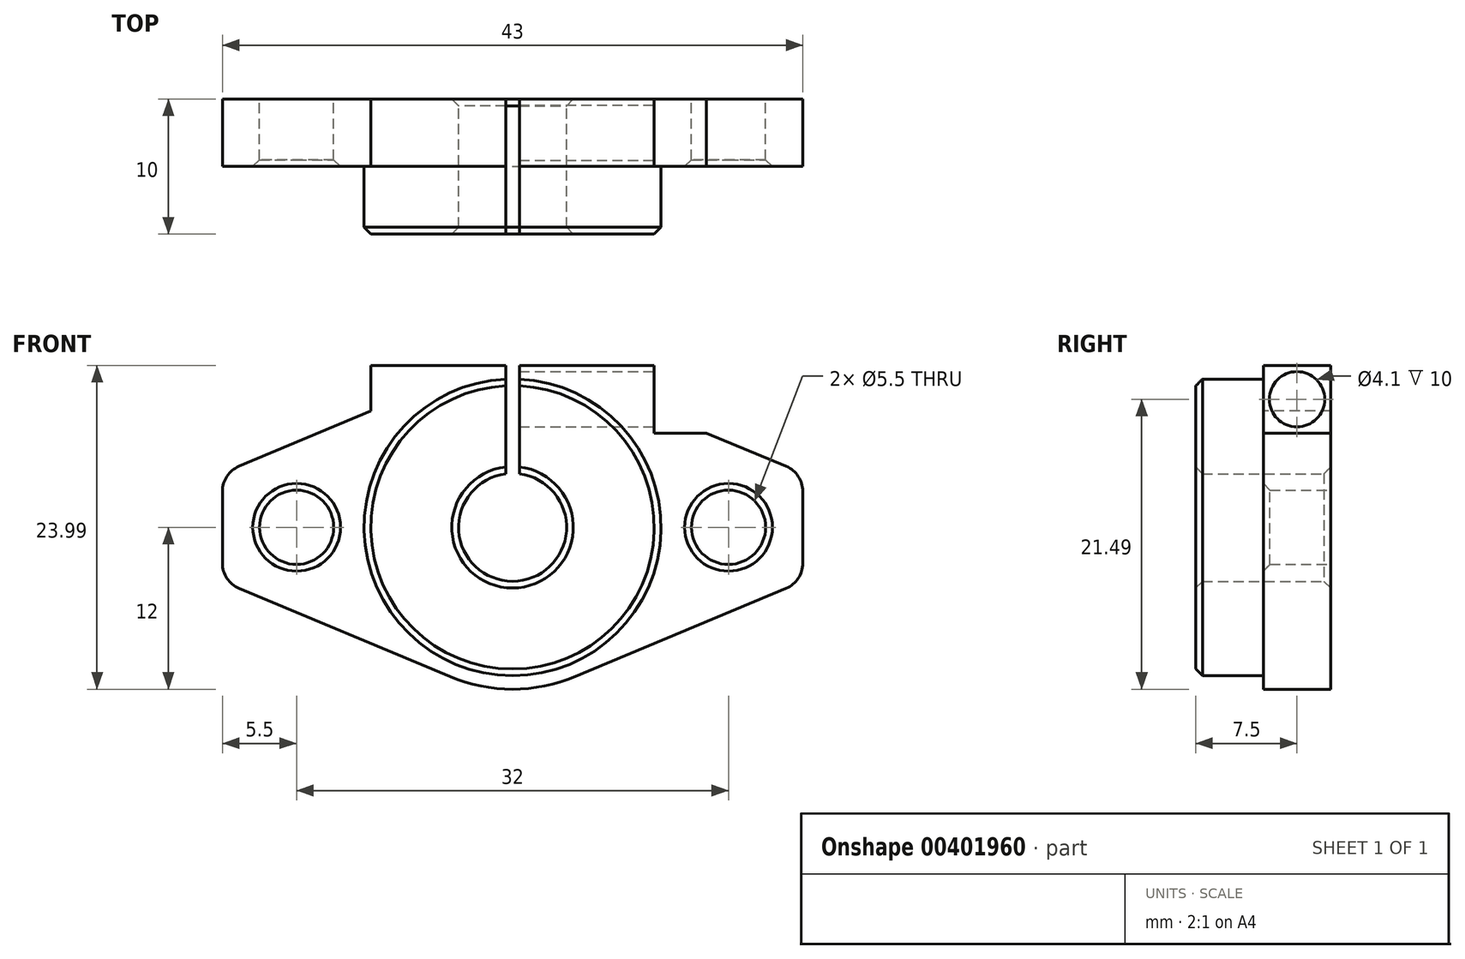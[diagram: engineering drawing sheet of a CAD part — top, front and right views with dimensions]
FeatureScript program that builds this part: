
annotation { "Feature Type Name" : "Feature", "Feature Type Description" : "" }
export const myFeature = defineFeature(function(context is Context, id is Id, definition is map)
    precondition{}
    {
        {
            var Q0;
            Q0=qCreatedBy(makeId("Front.planeOp"),FACE);
            var sketch = newSketch(context, id + "F0", { "sketchPlane" : qUnion([Q0])});
            skLineSegment(sketch, "E0.bottom", {"start": v(-21.5, 12) * mm, "end": v(21.5, 12) * mm, "construction": true});
            skLineSegment(sketch, "E0.top", {"start": v(-21.5, -12) * mm, "end": v(21.5, -12) * mm, "construction": true});
            skLineSegment(sketch, "E0.left", {"start": v(-21.5, 12) * mm, "end": v(-21.5, -12) * mm, "construction": true});
            skLineSegment(sketch, "E0.right", {"start": v(21.5, 12) * mm, "end": v(21.5, -12) * mm, "construction": true});
            skLineSegment(sketch, "E1", {"start": v(0, 0) * mm, "end": v(0, 12) * mm, "construction": true});
            skLineSegment(sketch, "E2", {"start": v(0, 0) * mm, "end": v(-21.5, 0) * mm, "construction": true});
            skCircle(sketch, "E3", {"center": v(-16, 0) * mm, "radius": 2.75 * mm});
            skCircle(sketch, "E4.MirrorC", {"center": v(16, 0) * mm, "radius": 2.75 * mm});
            skLineSegment(sketch, "E5", {"start": v(-21.5, -4) * mm, "end": v(-21.5, 4) * mm});
            skCircle(sketch, "E6", {"center": v(0, 0) * mm, "radius": 4 * mm});
            skArc(sketch, "E7", {"start": v(-4.64, -11.07) * mm, "mid": v(0, -12) * mm, "end": v(4.64, -11.07) * mm});
            skLineSegment(sketch, "E8", {"start": v(-21.5, 4) * mm, "end": v(-4.64, 11.07) * mm});
            skLineSegment(sketch, "E9", {"start": v(-21.5, -4) * mm, "end": v(-4.64, -11.07) * mm});
            skLineSegment(sketch, "E10.MirrorCS", {"start": v(21.5, 4) * mm, "end": v(4.64, 11.07) * mm});
            skLineSegment(sketch, "E11.MirrorCS", {"start": v(21.5, -4) * mm, "end": v(21.5, 4) * mm});
            skLineSegment(sketch, "E12.MirrorCS", {"start": v(21.5, -4) * mm, "end": v(4.64, -11.07) * mm});
            skArc(sketch, "E13.trimOffspring", {"start": v(4.64, 11.07) * mm, "mid": v(0, 12) * mm, "end": v(-4.64, 11.07) * mm});
            skSolve(sketch);
        }
        {
            var Q0;
            Q0=makeQuery(id+"F0.imprint","IMPRINT",FACE,{"disambiguationData":[TD([[makeQuery(id+"F0.imprint","IMPRINT",EDGE,{"derivedFrom":sQuery(id+"F0.wireOp",EDGE,"E3")}),-1.0]])]});
            extrude(context, id + "F1", {"entities" : qUnion([Q0]), "depth" : 5 * mm});
        }
        {
            var Q0;
            Q0=makeQuery(id+"F1.opExtrude","CAP_FACE",FACE,{"disambiguationData":[OSD([sQuery(id+"F0.wireOp",EDGE,"E3"),sQuery(id+"F0.wireOp",EDGE,"E4.MirrorC"),sQuery(id+"F0.wireOp",EDGE,"E5"),sQuery(id+"F0.wireOp",EDGE,"E6"),sQuery(id+"F0.wireOp",EDGE,"E7"),sQuery(id+"F0.wireOp",EDGE,"E8"),sQuery(id+"F0.wireOp",EDGE,"E9"),sQuery(id+"F0.wireOp",EDGE,"E10.MirrorCS"),sQuery(id+"F0.wireOp",EDGE,"E11.MirrorCS"),sQuery(id+"F0.wireOp",EDGE,"E12.MirrorCS"),sQuery(id+"F0.wireOp",EDGE,"E13.trimOffspring")])],"isStart":false});
            var sketch = newSketch(context, id + "F2", { "sketchPlane" : qUnion([Q0])});
            skCircle(sketch, "E14", {"center": v(0, 0) * mm, "radius": 11 * mm});
            skCircle(sketch, "E15.0", {"center": v(0, 0) * mm, "radius": 4 * mm});
            skSolve(sketch);
        }
        {
            var Q0;
            Q0 = qSketchRegion(id + "F2", true);
            extrude(context, id + "F3", {"entities" : qUnion([Q0]), "operationType" : NewBodyOperationType.ADD, "depth" : 5 * mm});
        }
        {
            var Q0;
            Q0=makeQuery(id+"F3.opExtrude","CAP_FACE",FACE,{"disambiguationData":[OSD([sQuery(id+"F2.wireOp",EDGE,"E14"),sQuery(id+"F2.wireOp",EDGE,"E15.0")])],"isStart":false});
            var sketch = newSketch(context, id + "F4", { "sketchPlane" : qUnion([Q0])});
            skLineSegment(sketch, "E16.bottom", {"start": v(-0.5, 18) * mm, "end": v(0.5, 18) * mm});
            skLineSegment(sketch, "E16.top", {"start": v(-0.5, 0) * mm, "end": v(0.5, 0) * mm});
            skLineSegment(sketch, "E16.left", {"start": v(-0.5, 18) * mm, "end": v(-0.5, 0) * mm});
            skLineSegment(sketch, "E16.right", {"start": v(0.5, 18) * mm, "end": v(0.5, 0) * mm});
            skSolve(sketch);
        }
        {
            var Q0;
            Q0 = qSketchRegion(id + "F4", true);
            extrude(context, id + "F5", {"entities" : qUnion([Q0]), "operationType" : NewBodyOperationType.REMOVE, "endBound" : BoundingType.THROUGH_ALL, "oppositeDirection" : true, "depth" : 25 * mm});
        }
        {
            var Q0;
            {var subQ0=sQuery(id+"F0.wireOp",EDGE,"E8");var subQ1=sQuery(id+"F0.wireOp",EDGE,"E7");var subQ2=sQuery(id+"F0.wireOp",EDGE,"E5");var subQ3=sQuery(id+"F0.wireOp",EDGE,"E3");var subQ4=sQuery(id+"F0.wireOp",EDGE,"E9");var subQ5=sQuery(id+"F0.wireOp",EDGE,"E13.trimOffspring");Q0=makeQuery(id+"F3.boolean.opBoolean","SPLIT",FACE,{"disambiguationData":[TD([makeQuery(id+"F1.opExtrude","SWEPT_FACE",FACE,{"disambiguationData":[OSD([subQ3])]})])],"derivedFrom":makeQuery(id+"F1.opExtrude","CAP_FACE",FACE,{"disambiguationData":[OSD([subQ3,sQuery(id+"F0.wireOp",EDGE,"E4.MirrorC"),subQ2,sQuery(id+"F0.wireOp",EDGE,"E6"),subQ1,subQ0,subQ4,sQuery(id+"F0.wireOp",EDGE,"E10.MirrorCS"),sQuery(id+"F0.wireOp",EDGE,"E11.MirrorCS"),sQuery(id+"F0.wireOp",EDGE,"E12.MirrorCS"),subQ5])],"isStart":false})});}
            var sketch = newSketch(context, id + "F6", { "sketchPlane" : qUnion([Q0])});
            skLineSegment(sketch, "E17.bottom", {"start": v(-10.5, 11.99) * mm, "end": v(-0.5, 11.99) * mm});
            skLineSegment(sketch, "E17.top", {"start": v(-10.5, 3.97) * mm, "end": v(-0.5, 3.97) * mm});
            skLineSegment(sketch, "E17.left", {"start": v(-10.5, 11.99) * mm, "end": v(-10.5, 3.97) * mm});
            skLineSegment(sketch, "E17.right", {"start": v(-0.5, 11.99) * mm, "end": v(-0.5, 3.97) * mm});
            skLineSegment(sketch, "E18", {"start": v(0, 0) * mm, "end": v(0, 14.34) * mm, "construction": true});
            skLineSegment(sketch, "E19.MirrorCS", {"start": v(0.5, 11.99) * mm, "end": v(0.5, 3.97) * mm});
            skLineSegment(sketch, "E20.MirrorCS", {"start": v(10.5, 11.99) * mm, "end": v(0.5, 11.99) * mm});
            skLineSegment(sketch, "E21.MirrorCS", {"start": v(10.5, 11.99) * mm, "end": v(10.5, 3.97) * mm});
            skLineSegment(sketch, "E22.MirrorCS", {"start": v(10.5, 3.97) * mm, "end": v(0.5, 3.97) * mm});
            skSolve(sketch);
        }
        {
            var Q0;
            Q0 = qSketchRegion(id + "F6", true);
            var Q1;
            Q1=makeQuery(id+"F1.opExtrude","CAP_FACE",FACE,{"disambiguationData":[OSD([sQuery(id+"F0.wireOp",EDGE,"E3"),sQuery(id+"F0.wireOp",EDGE,"E4.MirrorC"),sQuery(id+"F0.wireOp",EDGE,"E5"),sQuery(id+"F0.wireOp",EDGE,"E6"),sQuery(id+"F0.wireOp",EDGE,"E7"),sQuery(id+"F0.wireOp",EDGE,"E8"),sQuery(id+"F0.wireOp",EDGE,"E9"),sQuery(id+"F0.wireOp",EDGE,"E10.MirrorCS"),sQuery(id+"F0.wireOp",EDGE,"E11.MirrorCS"),sQuery(id+"F0.wireOp",EDGE,"E12.MirrorCS"),sQuery(id+"F0.wireOp",EDGE,"E13.trimOffspring")])],"isStart":true});
            extrude(context, id + "F7", {"entities" : qUnion([Q0]), "operationType" : NewBodyOperationType.ADD, "endBound" : BoundingType.UP_TO_SURFACE, "oppositeDirection" : true, "endBoundEntityFace" : qUnion([Q1]), "depth" : 25 * mm});
        }
        {
            var Q0;
            Q0=makeQuery(id+"F7.opExtrude","SWEPT_FACE",FACE,{"disambiguationData":[OSD([sQuery(id+"F6.wireOp",EDGE,"E21.MirrorCS")])]});
            var sketch = newSketch(context, id + "F8", { "sketchPlane" : qUnion([Q0])});
            skLineSegment(sketch, "E23.bottom", {"start": v(-5, 11.99) * mm, "end": v(0, 11.99) * mm});
            skLineSegment(sketch, "E23.top", {"start": v(-5, 6.99) * mm, "end": v(0, 6.99) * mm});
            skLineSegment(sketch, "E23.left", {"start": v(-5, 11.99) * mm, "end": v(-5, 6.99) * mm});
            skLineSegment(sketch, "E23.right", {"start": v(0, 11.99) * mm, "end": v(0, 6.99) * mm});
            skSolve(sketch);
        }
        {
            var Q0;
            Q0 = qSketchRegion(id + "F8", true);
            extrude(context, id + "F9", {"entities" : qUnion([Q0]), "operationType" : NewBodyOperationType.REMOVE, "endBound" : BoundingType.THROUGH_ALL, "depth" : 25 * mm});
        }
        {
            var Q0;
            Q0=makeQuery(id+"F9.boolean.opBoolean","MERGE",FACE,{"derivedFrom":[makeQuery(id+"F7.opExtrude","SWEPT_FACE",FACE,{"disambiguationData":[OSD([sQuery(id+"F6.wireOp",EDGE,"E21.MirrorCS")])]}),makeQuery(id+"F9.opExtrude","CAP_FACE",FACE,{"disambiguationData":[OSD([sQuery(id+"F8.wireOp",EDGE,"E23.bottom"),sQuery(id+"F8.wireOp",EDGE,"E23.top"),sQuery(id+"F8.wireOp",EDGE,"E23.left"),sQuery(id+"F8.wireOp",EDGE,"E23.right")])],"isStart":true})]});
            var sketch = newSketch(context, id + "F10", { "sketchPlane" : qUnion([Q0])});
            skLineSegment(sketch, "E24", {"start": v(-5, 9.49) * mm, "end": v(0, 9.49) * mm, "construction": true});
            skPoint(sketch, "E25", {"position": v(-2.5, 9.49) * mm});
            skCircle(sketch, "E26", {"center": v(-2.5, 9.49) * mm, "radius": 2.05 * mm});
            skSolve(sketch);
        }
        {
            var Q0;
            Q0=makeQuery(id+"F10.imprint","IMPRINT",FACE,{"disambiguationData":[TD([[makeQuery(id+"F10.imprint","IMPRINT",EDGE,{"derivedFrom":sQuery(id+"F10.wireOp",EDGE,"E26")}),1.0]])]});
            var Q1;
            Q1=makeQuery(id+"F5.boolean.opBoolean","COPY",FACE,{"derivedFrom":makeQuery(id+"F5.opExtrude","SWEPT_FACE",FACE,{"disambiguationData":[OSD([sQuery(id+"F4.wireOp",EDGE,"E16.left")])]})});
            extrude(context, id + "F11", {"entities" : qUnion([Q0]), "operationType" : NewBodyOperationType.REMOVE, "endBound" : BoundingType.UP_TO_SURFACE, "oppositeDirection" : true, "endBoundEntityFace" : qUnion([Q1]), "depth" : 25 * mm});
        }
        {
            var Q0;
            Q0=makeQuery(id+"F1.opExtrude","CAP_EDGE",EDGE,{"disambiguationData":[OSD([sQuery(id+"F0.wireOp",EDGE,"E6")])],"isStart":true});
            var Q1;
            Q1=makeQuery(id+"F3.opExtrude","CAP_EDGE",EDGE,{"disambiguationData":[OSD([sQuery(id+"F2.wireOp",EDGE,"E15.0")])],"isStart":false});
            var Q2;
            Q2=makeQuery(id+"F3.opExtrude","CAP_EDGE",EDGE,{"disambiguationData":[OSD([sQuery(id+"F2.wireOp",EDGE,"E14")])],"isStart":false});
            var Q3;
            Q3=makeQuery(id+"F1.opExtrude","CAP_EDGE",EDGE,{"disambiguationData":[OSD([sQuery(id+"F0.wireOp",EDGE,"E4.MirrorC")])],"isStart":false});
            var Q4;
            Q4=makeQuery(id+"F1.opExtrude","CAP_EDGE",EDGE,{"disambiguationData":[OSD([sQuery(id+"F0.wireOp",EDGE,"E3")])],"isStart":false});
            chamfer(context, id + "F12", {"entities" : qUnion([Q0, Q1, Q2, Q3, Q4]), "width" : 0.5 * mm, "tangentPropagation" : true});
        }
        {
            var Q0;
            Q0=makeQuery(id+"F1.opExtrude","SWEPT_EDGE",EDGE,{"disambiguationData":[OSD([sQuery(id+"F0.wireOp",EDGE,"E11.MirrorCS"),sQuery(id+"F0.wireOp",EDGE,"E12.MirrorCS")])]});
            var Q1;
            Q1=makeQuery(id+"F1.opExtrude","SWEPT_EDGE",EDGE,{"disambiguationData":[OSD([sQuery(id+"F0.wireOp",EDGE,"E10.MirrorCS"),sQuery(id+"F0.wireOp",EDGE,"E11.MirrorCS")])]});
            var Q2;
            Q2=makeQuery(id+"F1.opExtrude","SWEPT_EDGE",EDGE,{"disambiguationData":[OSD([sQuery(id+"F0.wireOp",EDGE,"E5"),sQuery(id+"F0.wireOp",EDGE,"E9")])]});
            var Q3;
            Q3=makeQuery(id+"F1.opExtrude","SWEPT_EDGE",EDGE,{"disambiguationData":[OSD([sQuery(id+"F0.wireOp",EDGE,"E5"),sQuery(id+"F0.wireOp",EDGE,"E8")])]});
            fillet(context, id + "F13", {"entities" : qUnion([Q0, Q1, Q2, Q3]), "radius" : 2 * mm, "tangentPropagation" : true, "allowEdgeOverflow" : false});
        }
    });
